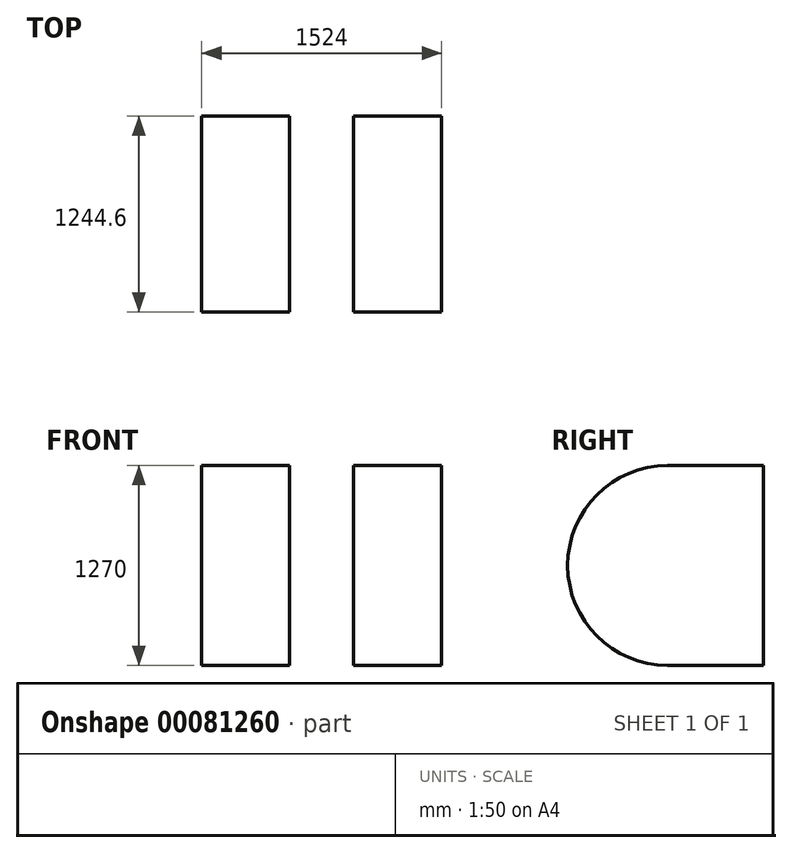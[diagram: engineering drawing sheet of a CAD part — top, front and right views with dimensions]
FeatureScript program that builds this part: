
annotation { "Feature Type Name" : "Feature", "Feature Type Description" : "" }
export const myFeature = defineFeature(function(context is Context, id is Id, definition is map)
    precondition{}
    {
        {
            var Q0;
            Q0=qCreatedBy(makeId("Top.planeOp"),FACE);
            var sketch = newSketch(context, id + "F0", { "sketchPlane" : qUnion([Q0])});
            skLineSegment(sketch, "E0.bottom", {"start": v(0, 0) * mm, "end": v(1524, 0) * mm});
            skLineSegment(sketch, "E0.top", {"start": v(0, -2794) * mm, "end": v(1524, -2794) * mm});
            skLineSegment(sketch, "E0.left", {"start": v(0, 0) * mm, "end": v(0, -2794) * mm});
            skLineSegment(sketch, "E0.right", {"start": v(1524, 0) * mm, "end": v(1524, -2794) * mm});
            skLineSegment(sketch, "E1.top", {"start": v(0, -2794) * mm, "end": v(558.8, -2794) * mm});
            skLineSegment(sketch, "E1.left", {"start": v(0, -2235.2) * mm, "end": v(0, -2794) * mm});
            skLineSegment(sketch, "E1.right", {"start": v(558.8, -1549.4) * mm, "end": v(558.8, -2794) * mm});
            skLineSegment(sketch, "E2.bottom", {"start": v(965.2, -2794) * mm, "end": v(1524, -2794) * mm});
            skLineSegment(sketch, "E2.top", {"start": v(965.2, -1549.4) * mm, "end": v(1524, -1549.4) * mm});
            skLineSegment(sketch, "E2.left", {"start": v(965.2, -2794) * mm, "end": v(965.2, -1549.4) * mm});
            skLineSegment(sketch, "E2.right", {"start": v(1524, -2794) * mm, "end": v(1524, -1549.4) * mm});
            skLineSegment(sketch, "E3.bottom", {"start": v(381, 0) * mm, "end": v(1143, 0) * mm});
            skLineSegment(sketch, "E3.top", {"start": v(381, -1244.6) * mm, "end": v(1143, -1244.6) * mm});
            skLineSegment(sketch, "E3.left", {"start": v(381, 0) * mm, "end": v(381, -1244.6) * mm});
            skLineSegment(sketch, "E3.right", {"start": v(1143, 0) * mm, "end": v(1143, -1244.6) * mm});
            skLineSegment(sketch, "E4", {"start": v(558.8, -1549.4) * mm, "end": v(0, -1549.4) * mm});
            skSolve(sketch);
        }
        {
            var Q0;
            Q0=makeQuery(id+"F0.imprint","IMPRINT",FACE,{"disambiguationData":[TD([[makeQuery(id+"F0.imprint","IMPRINT",EDGE,{"derivedFrom":sQuery(id+"F0.wireOp",EDGE,"E0.top")}),1.0]])]});
            extrude(context, id + "F1", {"entities" : qUnion([Q0]), "depth" : 1270 * mm});
        }
        {
            var Q0;
            {var subQ0=sQuery(id+"F0.wireOp",EDGE,"E0.bottom");Q0=makeQuery(id+"F1.opExtrude","CAP_EDGE",EDGE,{"disambiguationData":[OSD([subQ0]),TDD([makeQuery(id+"F0.imprint","IMPRINT",EDGE,{"disambiguationData":[TD([[makeQuery(id+"F0.imprint","INTERSECT",VERTEX,{"derivedFrom":[subQ0,sQuery(id+"F0.wireOp",EDGE,"E0.left")]}),-1.0]])],"derivedFrom":subQ0})])],"isStart":false});}
            var Q1;
            {var subQ0=sQuery(id+"F0.wireOp",EDGE,"E0.bottom");Q1=makeQuery(id+"F1.opExtrude","CAP_EDGE",EDGE,{"disambiguationData":[OSD([subQ0]),TDD([makeQuery(id+"F0.imprint","IMPRINT",EDGE,{"disambiguationData":[TD([[makeQuery(id+"F0.imprint","INTERSECT",VERTEX,{"derivedFrom":[subQ0,sQuery(id+"F0.wireOp",EDGE,"E0.left")]}),-1.0]])],"derivedFrom":subQ0})])],"isStart":true});}
            var Q2;
            {var subQ0=sQuery(id+"F0.wireOp",EDGE,"E0.bottom");Q2=makeQuery(id+"F1.opExtrude","CAP_EDGE",EDGE,{"disambiguationData":[OSD([subQ0]),TDD([makeQuery(id+"F0.imprint","IMPRINT",EDGE,{"disambiguationData":[TD([[makeQuery(id+"F0.imprint","INTERSECT",VERTEX,{"derivedFrom":[subQ0,sQuery(id+"F0.wireOp",EDGE,"E0.right")]}),1.0]])],"derivedFrom":subQ0})])],"isStart":false});}
            var Q3;
            {var subQ0=sQuery(id+"F0.wireOp",EDGE,"E0.bottom");Q3=makeQuery(id+"F1.opExtrude","CAP_EDGE",EDGE,{"disambiguationData":[OSD([subQ0]),TDD([makeQuery(id+"F0.imprint","IMPRINT",EDGE,{"disambiguationData":[TD([[makeQuery(id+"F0.imprint","INTERSECT",VERTEX,{"derivedFrom":[subQ0,sQuery(id+"F0.wireOp",EDGE,"E0.right")]}),1.0]])],"derivedFrom":subQ0})])],"isStart":true});}
            var Q4;
            Q4=makeQuery(id+"F1.opExtrude","CAP_EDGE",EDGE,{"disambiguationData":[OSD([sQuery(id+"F0.wireOp",EDGE,"E0.top")])],"isStart":false});
            var Q5;
            Q5=makeQuery(id+"F1.opExtrude","CAP_EDGE",EDGE,{"disambiguationData":[OSD([sQuery(id+"F0.wireOp",EDGE,"E0.top")])],"isStart":true});
            fillet(context, id + "F2", {"entities" : qUnion([Q0, Q1, Q2, Q3, Q4, Q5]), "radius" : 635 * mm, "tangentPropagation" : true, "allowEdgeOverflow" : false});
        }
        {
            var Q0;
            Q0=makeQuery(id+"F1.opExtrude","SWEPT_FACE",FACE,{"disambiguationData":[OSD([sQuery(id+"F0.wireOp",EDGE,"E1.right")])]});
            var sketch = newSketch(context, id + "F3", { "sketchPlane" : qUnion([Q0])});
            skPoint(sketch, "E5", {"position": v(2463.8, 635) * mm});
            skPoint(sketch, "E5.positionSnap0", {"position": v(2794, 635) * mm});
            skSolve(sketch);
        }
        {
            var Q0;
            Q0=sQuery(id+"F3.wireOp",VERTEX,"E5");
            var Q1;
            Q1=makeQuery(id+"F1.opExtrude","SWEPT_BODY",BODY,{"disambiguationData":[OSD([sQuery(id+"F0.wireOp",EDGE,"E0.bottom"),sQuery(id+"F0.wireOp",EDGE,"E0.top"),sQuery(id+"F0.wireOp",EDGE,"E0.left"),sQuery(id+"F0.wireOp",EDGE,"E0.right"),sQuery(id+"F0.wireOp",EDGE,"E1.right"),sQuery(id+"F0.wireOp",EDGE,"E2.top"),sQuery(id+"F0.wireOp",EDGE,"E2.left"),sQuery(id+"F0.wireOp",EDGE,"E3.top"),sQuery(id+"F0.wireOp",EDGE,"E3.left"),sQuery(id+"F0.wireOp",EDGE,"E3.right"),sQuery(id+"F0.wireOp",EDGE,"E4")])]});
            hole(context, id + "F4", {"style" : HoleStyle.SIMPLE, "endStyle" : HoleEndStyle.THROUGH, "holeDiameter" : 317.5 * mm, "locations" : qUnion([Q0]), "scope" : qUnion([Q1]), "isTappedThrough" : true});
        }
        {
            var Q0;
            Q0=makeQuery(id+"F1.opExtrude","SWEPT_FACE",FACE,{"disambiguationData":[OSD([sQuery(id+"F0.wireOp",EDGE,"E0.right")])]});
            var sketch = newSketch(context, id + "F5", { "sketchPlane" : qUnion([Q0])});
            skPoint(sketch, "E6", {"position": v(-635, 635) * mm});
            skPoint(sketch, "E6.positionSnap0", {"position": v(0, 635) * mm});
            skSolve(sketch);
        }
        {
            var Q0;
            Q0=sQuery(id+"F5.wireOp",VERTEX,"E6");
            var Q1;
            Q1=makeQuery(id+"F1.opExtrude","SWEPT_BODY",BODY,{"disambiguationData":[OSD([sQuery(id+"F0.wireOp",EDGE,"E0.bottom"),sQuery(id+"F0.wireOp",EDGE,"E0.top"),sQuery(id+"F0.wireOp",EDGE,"E0.left"),sQuery(id+"F0.wireOp",EDGE,"E0.right"),sQuery(id+"F0.wireOp",EDGE,"E1.right"),sQuery(id+"F0.wireOp",EDGE,"E2.top"),sQuery(id+"F0.wireOp",EDGE,"E2.left"),sQuery(id+"F0.wireOp",EDGE,"E3.top"),sQuery(id+"F0.wireOp",EDGE,"E3.left"),sQuery(id+"F0.wireOp",EDGE,"E3.right"),sQuery(id+"F0.wireOp",EDGE,"E4")])]});
            hole(context, id + "F6", {"style" : HoleStyle.SIMPLE, "endStyle" : HoleEndStyle.THROUGH, "holeDiameter" : 317.5 * mm, "locations" : qUnion([Q0]), "scope" : qUnion([Q1]), "isTappedThrough" : true});
        }
    });
